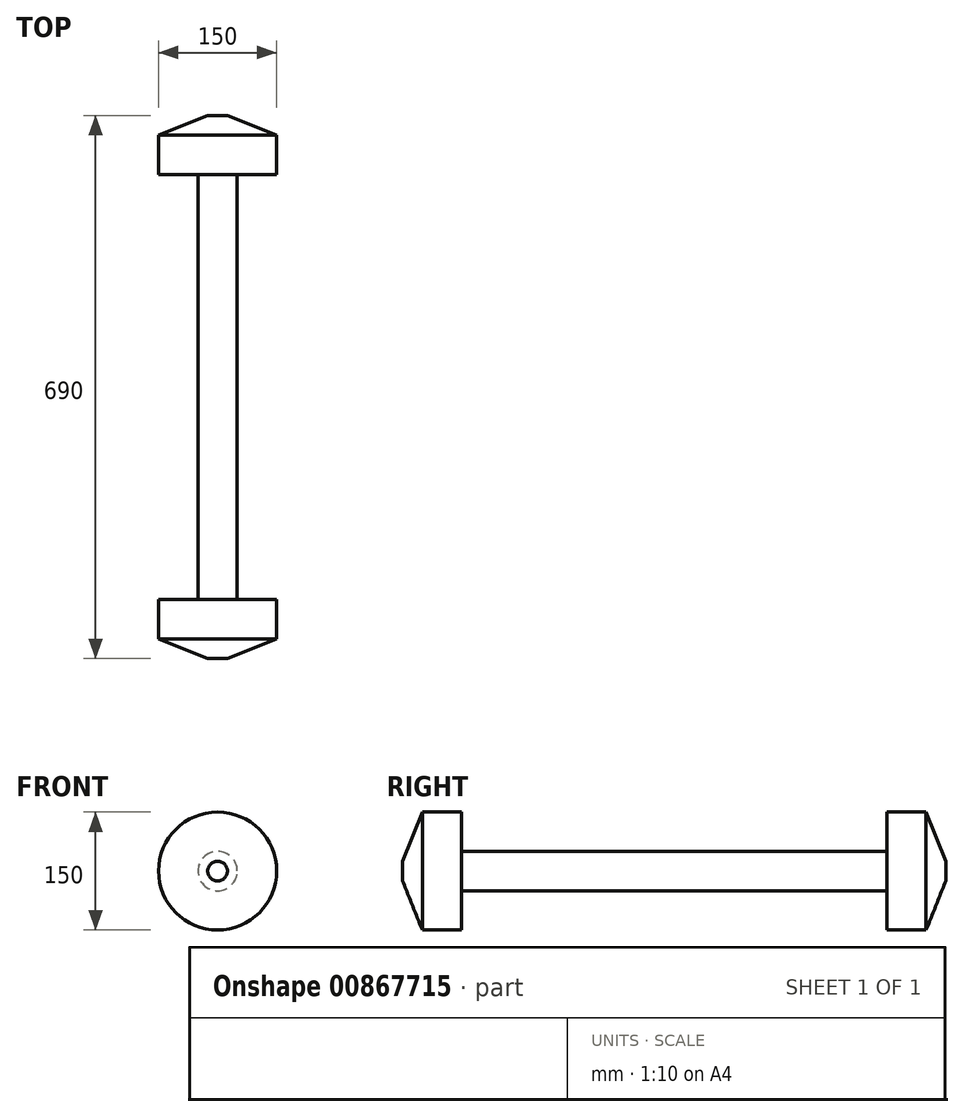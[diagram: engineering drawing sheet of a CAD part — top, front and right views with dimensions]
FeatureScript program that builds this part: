
annotation { "Feature Type Name" : "Feature", "Feature Type Description" : "" }
export const myFeature = defineFeature(function(context is Context, id is Id, definition is map)
    precondition{}
    {
        {
            var Q0;
            Q0=qCreatedBy(makeId("Front.planeOp"),FACE);
            var sketch = newSketch(context, id + "F0", { "sketchPlane" : qUnion([Q0])});
            skCircle(sketch, "E0", {"center": v(0, 0) * mm, "radius": 25 * mm});
            skSolve(sketch);
        }
        {
            var Q0;
            Q0=qSketchRegion(id+"F0",true);
            extrude(context, id + "F1", {"entities" : qUnion([Q0]), "depth" : 270 * mm, "offsetDistance" : 25 * mm});
        }
        {
            var Q0;
            Q0=makeQuery(id+"F1.opExtrude","CAP_FACE",FACE,{"disambiguationData":[OSD([sQuery(id+"F0.wireOp",EDGE,"E0")])],"isStart":false});
            var sketch = newSketch(context, id + "F2", { "sketchPlane" : qUnion([Q0])});
            skCircle(sketch, "E1", {"center": v(0, 0) * mm, "radius": 75 * mm});
            skSolve(sketch);
        }
        {
            var Q0;
            Q0=qSketchRegion(id+"F2",true);
            extrude(context, id + "F3", {"entities" : qUnion([Q0]), "operationType" : NewBodyOperationType.ADD, "depth" : 50 * mm, "offsetDistance" : 25 * mm});
        }
        {
            var Q0;
            Q0=makeQuery(id+"F1.opExtrude","SWEPT_BODY",BODY,{"disambiguationData":[OSD([sQuery(id+"F0.wireOp",EDGE,"E0")])]});
            var Q1;
            Q1=qCreatedBy(makeId("Front.planeOp"),FACE);
            mirror(context, id + "F4", {"operationType" : NewBodyOperationType.ADD, "entities" : qUnion([Q0]), "mirrorPlane" : qUnion([Q1])});
        }
        {
            var Q0;
            Q0=makeQuery(id+"F3.opExtrude","CAP_FACE",FACE,{"disambiguationData":[OSD([sQuery(id+"F2.wireOp",EDGE,"E1")])],"isStart":false});
            cPlane(context, id + "F5", {"entities" : qUnion([Q0]), "cplaneType" : CPlaneType.OFFSET, "offset" : 25 * mm, "width" : 150 * mm, "height" : 150 * mm});
        }
        {
            var Q0;
            Q0=qCreatedBy(id+"F5.planeOp",FACE);
            var sketch = newSketch(context, id + "F6", { "sketchPlane" : qUnion([Q0])});
            skCircle(sketch, "E2", {"center": v(0, 0) * mm, "radius": 12.5 * mm});
            skSolve(sketch);
        }
        {
            var Q1;
            Q1=makeQuery(id+"F3.opExtrude","CAP_FACE",FACE,{"disambiguationData":[OSD([sQuery(id+"F2.wireOp",EDGE,"E1")])],"isStart":false});
            var Q2;
            Q2=makeQuery(id+"F6.imprint","IMPRINT",FACE,{"disambiguationData":[TD([[makeQuery(id+"F6.imprint","IMPRINT",EDGE,{"derivedFrom":sQuery(id+"F6.wireOp",EDGE,"E2")}),1.0]])]});
            loft(context, id + "F7", {"operationType" : NewBodyOperationType.ADD, "sheetProfilesArray" : [{ "sheetProfileEntities" : qUnion([Q1]) }, { "sheetProfileEntities" : qUnion([Q2]) }]});
        }
        {
            var Q0;
            Q0=makeQuery(id+"F4.opPattern","COPY",FACE,{"derivedFrom":makeQuery(id+"F3.opExtrude","CAP_FACE",FACE,{"disambiguationData":[OSD([sQuery(id+"F2.wireOp",EDGE,"E1")])],"isStart":false}),"instanceName":"1"});
            cPlane(context, id + "F8", {"entities" : qUnion([Q0]), "cplaneType" : CPlaneType.OFFSET, "offset" : 25 * mm, "width" : 150 * mm, "height" : 150 * mm});
        }
        {
            var Q0;
            Q0=qCreatedBy(id+"F8.planeOp",FACE);
            var sketch = newSketch(context, id + "F9", { "sketchPlane" : qUnion([Q0])});
            skCircle(sketch, "E3", {"center": v(0, 0) * mm, "radius": 12.5 * mm});
            skSolve(sketch);
        }
        {
            var Q1;
            Q1=makeQuery(id+"F9.imprint","IMPRINT",FACE,{"disambiguationData":[TD([[makeQuery(id+"F9.imprint","IMPRINT",EDGE,{"derivedFrom":sQuery(id+"F9.wireOp",EDGE,"E3")}),1.0]])]});
            var Q2;
            Q2=makeQuery(id+"F4.opPattern","COPY",FACE,{"derivedFrom":makeQuery(id+"F3.opExtrude","CAP_FACE",FACE,{"disambiguationData":[OSD([sQuery(id+"F2.wireOp",EDGE,"E1")])],"isStart":false}),"instanceName":"1"});
            loft(context, id + "F10", {"operationType" : NewBodyOperationType.ADD, "sheetProfilesArray" : [{ "sheetProfileEntities" : qUnion([Q1]) }, { "sheetProfileEntities" : qUnion([Q2]) }]});
        }
    });
